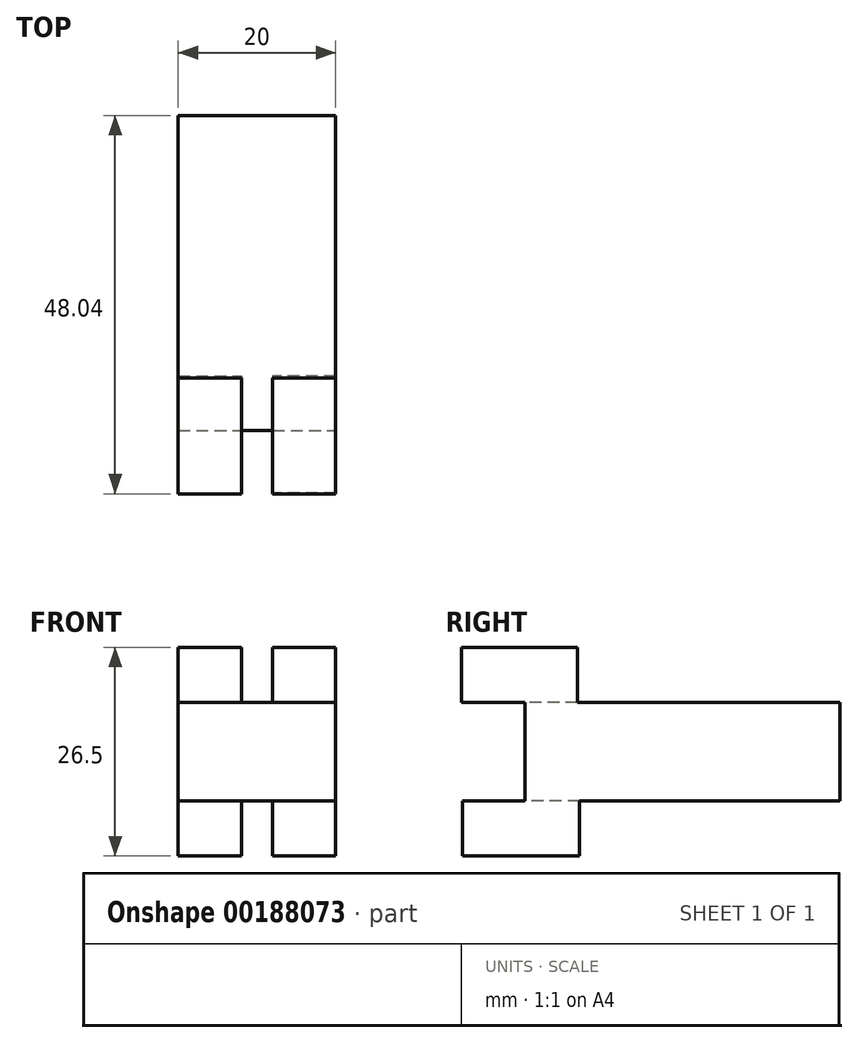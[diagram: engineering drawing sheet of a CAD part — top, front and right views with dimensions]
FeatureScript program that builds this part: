
annotation { "Feature Type Name" : "Feature", "Feature Type Description" : "" }
export const myFeature = defineFeature(function(context is Context, id is Id, definition is map)
    precondition{}
    {
        {
            var Q0;
            Q0=qCreatedBy(makeId("Front.planeOp"),FACE);
            var sketch = newSketch(context, id + "F0", { "sketchPlane" : qUnion([Q0])});
            skLineSegment(sketch, "E0.bottom", {"start": v(0, 0) * mm, "end": v(20, 0) * mm});
            skLineSegment(sketch, "E0.top", {"start": v(0, 12.5) * mm, "end": v(20, 12.5) * mm});
            skLineSegment(sketch, "E0.left", {"start": v(0, 0) * mm, "end": v(0, 12.5) * mm});
            skLineSegment(sketch, "E0.right", {"start": v(20, 0) * mm, "end": v(20, 12.5) * mm});
            skSolve(sketch);
        }
        {
            var Q0;
            Q0=makeQuery(id+"F0.imprint","IMPRINT",FACE,{"disambiguationData":[TD([[makeQuery(id+"F0.imprint","IMPRINT",EDGE,{"derivedFrom":sQuery(id+"F0.wireOp",EDGE,"E0.bottom")}),1.0]])]});
            extrude(context, id + "F1", {"entities" : qUnion([Q0]), "depth" : 40 * mm});
        }
        {
            var Q0;
            Q0=makeQuery(id+"F1.opExtrude","SWEPT_FACE",FACE,{"disambiguationData":[OSD([sQuery(id+"F0.wireOp",EDGE,"E0.top")])]});
            var sketch = newSketch(context, id + "F2", { "sketchPlane" : qUnion([Q0])});
            skLineSegment(sketch, "E1.bottom", {"start": v(0, -33.33) * mm, "end": v(8, -33.33) * mm});
            skLineSegment(sketch, "E1.top", {"start": v(0, -48.04) * mm, "end": v(8, -48.04) * mm});
            skLineSegment(sketch, "E1.left", {"start": v(0, -33.33) * mm, "end": v(0, -48.04) * mm});
            skLineSegment(sketch, "E1.right", {"start": v(8, -33.33) * mm, "end": v(8, -48.04) * mm});
            skLineSegment(sketch, "E2.bottom", {"start": v(20, -33.33) * mm, "end": v(12, -33.33) * mm});
            skLineSegment(sketch, "E2.top", {"start": v(20, -48.04) * mm, "end": v(12, -48.04) * mm});
            skLineSegment(sketch, "E2.left", {"start": v(20, -33.33) * mm, "end": v(20, -48.04) * mm});
            skLineSegment(sketch, "E2.right", {"start": v(12, -33.33) * mm, "end": v(12, -48.04) * mm});
            skSolve(sketch);
        }
        {
            var Q0;
            Q0 = qSketchRegion(id + "F2", true);
            extrude(context, id + "F3", {"entities" : qUnion([Q0]), "operationType" : NewBodyOperationType.ADD, "depth" : 7 * mm});
        }
        {
            var Q0;
            Q0=makeQuery(id+"F1.opExtrude","SWEPT_FACE",FACE,{"disambiguationData":[OSD([sQuery(id+"F0.wireOp",EDGE,"E0.bottom")])]});
            var sketch = newSketch(context, id + "F4", { "sketchPlane" : qUnion([Q0])});
            skLineSegment(sketch, "E3.bottom", {"start": v(0, 33.07) * mm, "end": v(8, 33.07) * mm});
            skLineSegment(sketch, "E3.top", {"start": v(0, 47.94) * mm, "end": v(8, 47.94) * mm});
            skLineSegment(sketch, "E3.left", {"start": v(0, 33.07) * mm, "end": v(0, 47.94) * mm});
            skLineSegment(sketch, "E3.right", {"start": v(8, 33.07) * mm, "end": v(8, 47.94) * mm});
            skLineSegment(sketch, "E4.bottom", {"start": v(20, 33.07) * mm, "end": v(12, 33.07) * mm});
            skLineSegment(sketch, "E4.top", {"start": v(20, 47.94) * mm, "end": v(12, 47.94) * mm});
            skLineSegment(sketch, "E4.left", {"start": v(20, 33.07) * mm, "end": v(20, 47.94) * mm});
            skLineSegment(sketch, "E4.right", {"start": v(12, 33.07) * mm, "end": v(12, 47.94) * mm});
            skSolve(sketch);
        }
        {
            var Q0;
            {var subQ0=sQuery(id+"F4.wireOp",EDGE,"E3.top");Q0=makeQuery(id+"F4.imprint","IMPRINT",FACE,{"disambiguationData":[TD([[makeQuery(id+"F4.imprint","IMPRINT",EDGE,{"derivedFrom":subQ0}),-1.0]])]});}
            var Q1;
            {var subQ0=sQuery(id+"F4.wireOp",EDGE,"E3.bottom");Q1=makeQuery(id+"F4.imprint","IMPRINT",FACE,{"disambiguationData":[TD([[makeQuery(id+"F4.imprint","IMPRINT",EDGE,{"derivedFrom":subQ0}),1.0]])]});}
            var Q2;
            {var subQ0=sQuery(id+"F4.wireOp",EDGE,"E4.bottom");Q2=makeQuery(id+"F4.imprint","IMPRINT",FACE,{"disambiguationData":[TD([[makeQuery(id+"F4.imprint","IMPRINT",EDGE,{"derivedFrom":subQ0}),-1.0]])]});}
            var Q3;
            {var subQ0=sQuery(id+"F4.wireOp",EDGE,"E4.top");Q3=makeQuery(id+"F4.imprint","IMPRINT",FACE,{"disambiguationData":[TD([[makeQuery(id+"F4.imprint","IMPRINT",EDGE,{"derivedFrom":subQ0}),1.0]])]});}
            extrude(context, id + "F5", {"entities" : qUnion([Q0, Q1, Q2, Q3]), "operationType" : NewBodyOperationType.ADD, "depth" : 7 * mm});
        }
    });
